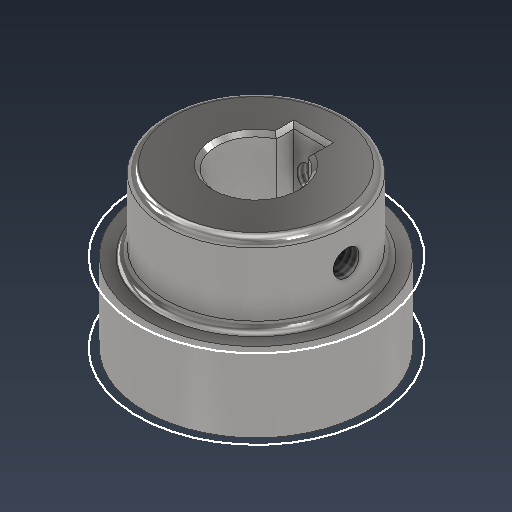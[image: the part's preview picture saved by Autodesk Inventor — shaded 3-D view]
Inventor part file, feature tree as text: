
AUTODESK INVENTOR PART (.ipt)
format: ipt  version: 2021 (Build 250183000, 183)  size: 236,032 bytes
history: native  units: mm
features: sketch x7, extrude x3, fillet x2, plane x2, hole x2, chamfer x1
ambient origin geometry x8: Origin, YZ Plane, XZ Plane, XY Plane, X Axis, Y Axis, Z Axis, Center Point
bodies: Solid1 (feature_tree)
feature tree (17):
  extrude  "Extrusion1"  Depth=10.0mm
  extrude  "Extrusion2"  Depth=10.0mm
  fillet  "Fillet1"  Radius=10.0mm
  plane  "Work Plane1"
  fillet  "Fillet2"  Radius=1.0mm
  plane  "Work Plane2"
  sketch  "Sketch4"  dims[d10=3.242mm d11=8.0mm d12=4.0mm d13=2.0mm d14=90.0deg d15=8.0mm d16=0.0mm d20=1.0mm]
  hole  "Hole1"  [1 undecoded]
  hole  "Hole2"  [1 undecoded]
  extrude  "Extrusion3"  TaperAngle=0.0deg  [1 undecoded]
  chamfer  "Chamfer2"  Distance=6.8mm
  sketch  "Sketch6"  dims[d23=3.242mm d24=8.0mm d25=4.0mm d26=2.0mm d27=90.0deg d28=8.0mm d29=0.0mm]
  sketch  "Sketch7"  dims[d30=4.0mm d31=6.8mm d32=0.0mm d33=0.0mm d34=0.5mm d35=2.0mm d36=45.0deg d37=30.0mm d38=30.0mm]
  sketch  "Sketch1"  dims[d0=10.0mm d1=28.0mm]
  sketch  "Sketch2"  dims[d2=10.0mm d3=0.0mm d4=23.0mm d5=10.0mm d6=0.0mm d7=1.0mm]
  sketch  "Sketch3"  dims[d8=5.0mm d9=0.0mm]
  sketch  "Sketch5"  dims[d21=5.0mm d22=0.0mm]
note: 3 required parameter values undecoded (feature->parameter linkage not recoverable at this tier; creation-order binding heuristic only, values carry confidence <= 0.55)
